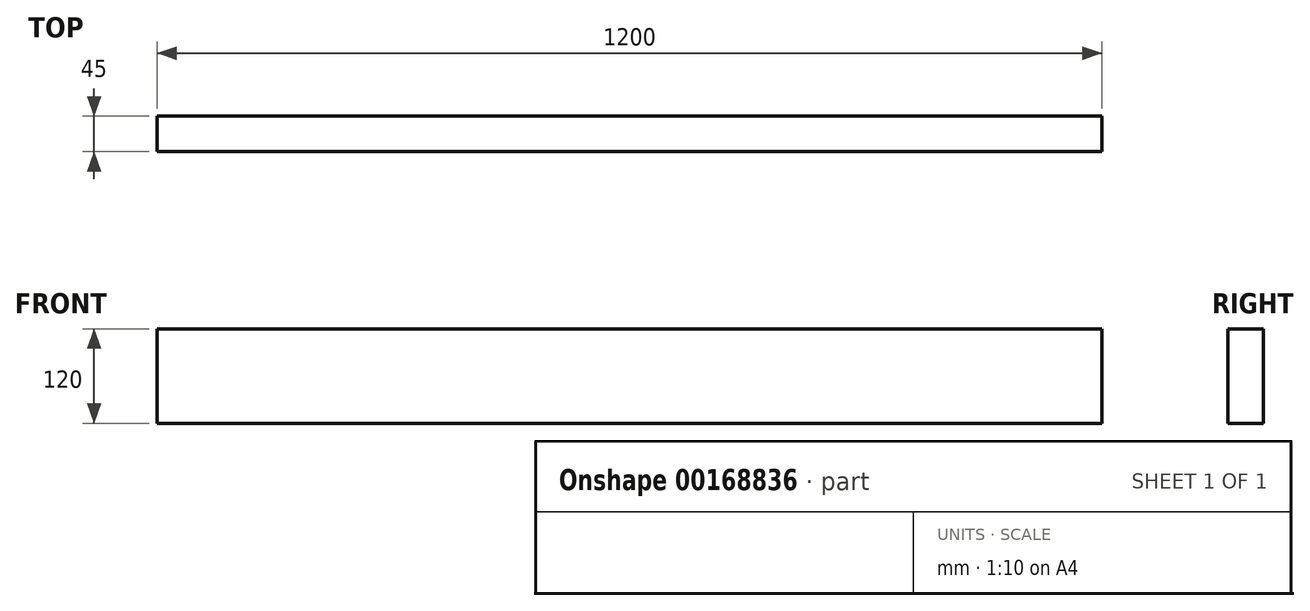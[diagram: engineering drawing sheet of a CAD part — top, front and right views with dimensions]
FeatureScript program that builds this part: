
annotation { "Feature Type Name" : "Feature", "Feature Type Description" : "" }
export const myFeature = defineFeature(function(context is Context, id is Id, definition is map)
    precondition{}
    {
        {
            var Q0;
            Q0=qCreatedBy(makeId("Right.planeOp"),FACE);
            var sketch = newSketch(context, id + "F0", { "sketchPlane" : qUnion([Q0])});
            skLineSegment(sketch, "E0.bottom", {"start": v(-22.5, 0) * mm, "end": v(22.5, 0) * mm});
            skLineSegment(sketch, "E0.top", {"start": v(-22.5, 120) * mm, "end": v(22.5, 120) * mm});
            skLineSegment(sketch, "E0.left", {"start": v(-22.5, 0) * mm, "end": v(-22.5, 120) * mm});
            skLineSegment(sketch, "E0.right", {"start": v(22.5, 0) * mm, "end": v(22.5, 120) * mm});
            skSolve(sketch);
        }
        {
            var Q0;
            Q0=makeQuery(id+"F0.imprint","IMPRINT",FACE,{"disambiguationData":[TD([[makeQuery(id+"F0.imprint","IMPRINT",EDGE,{"derivedFrom":sQuery(id+"F0.wireOp",EDGE,"E0.bottom")}),1.0]])]});
            extrude(context, id + "F1", {"entities" : qUnion([Q0]), "oppositeDirection" : true, "depth" : 1200 * mm});
        }
    });
